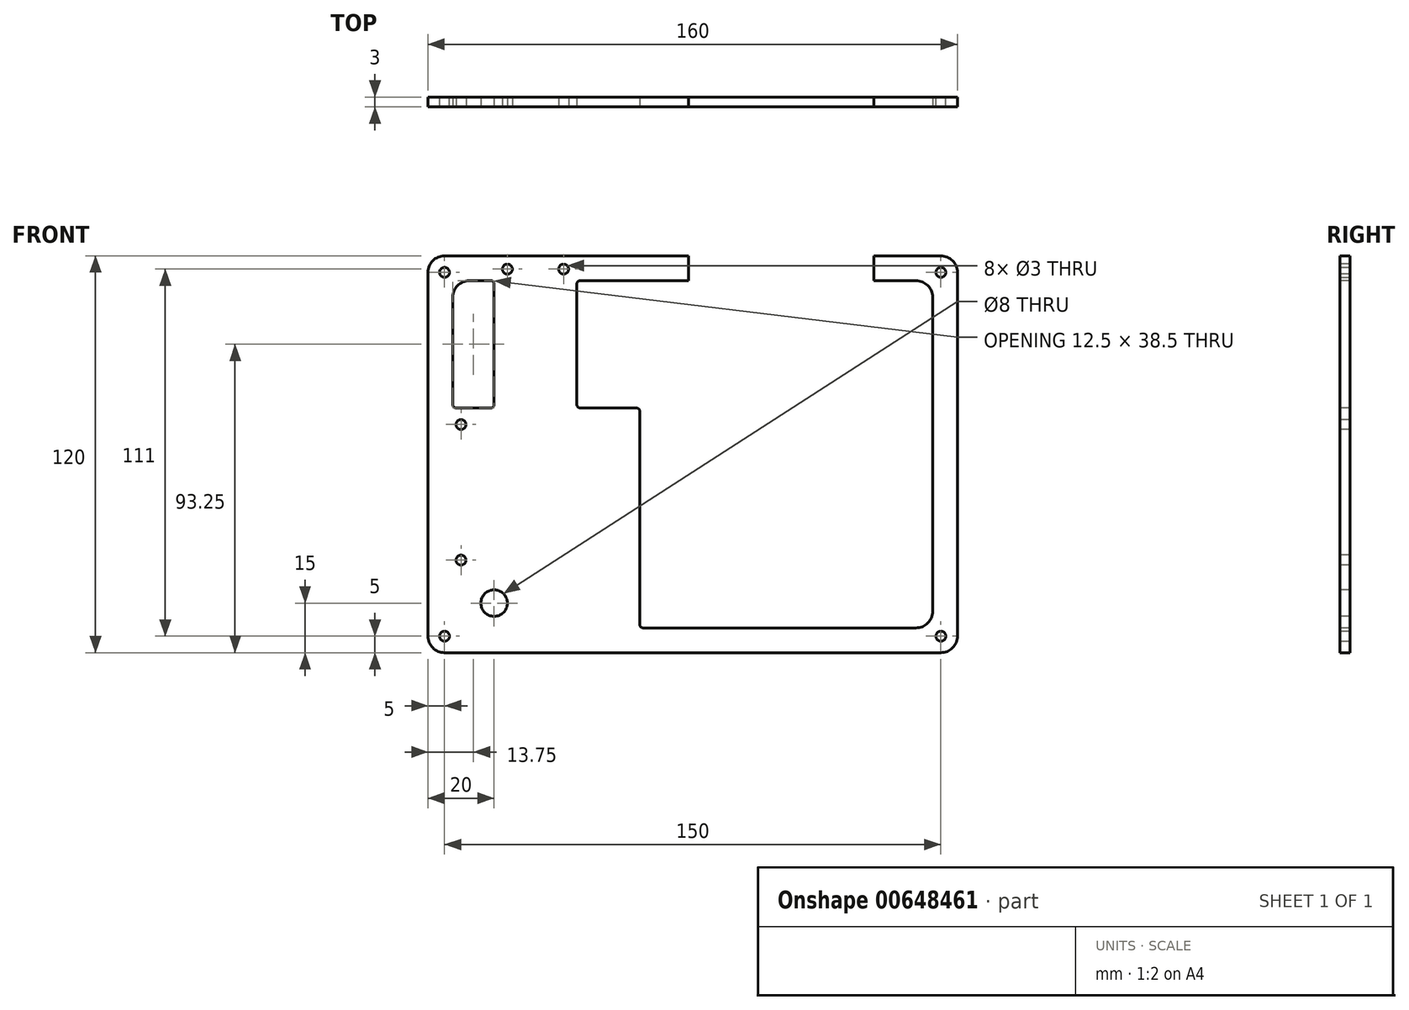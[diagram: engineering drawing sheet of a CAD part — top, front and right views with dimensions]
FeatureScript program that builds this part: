
annotation { "Feature Type Name" : "Feature", "Feature Type Description" : "" }
export const myFeature = defineFeature(function(context is Context, id is Id, definition is map)
    precondition{}
    {
        {
            var Q0;
            Q0=qCreatedBy(makeId("Front.planeOp"),FACE);
            var sketch = newSketch(context, id + "F0", { "sketchPlane" : qUnion([Q0])});
            skLineSegment(sketch, "E0.bottom", {"start": v(75, -60) * mm, "end": v(-75, -60) * mm});
            skLineSegment(sketch, "E0.top", {"start": v(75, 60) * mm, "end": v(-75, 60) * mm});
            skLineSegment(sketch, "E0.left", {"start": v(80, -55) * mm, "end": v(80, 55) * mm});
            skLineSegment(sketch, "E0.right", {"start": v(-80, -55) * mm, "end": v(-80, 55) * mm});
            skPoint(sketch, "E0.middle", {"position": v(0, 0) * mm});
            skPoint(sketch, "E1.visualSharp", {"position": v(-80, 60) * mm});
            skArc(sketch, "E1.filletArc", {"start": v(-75, 60) * mm, "mid": v(-78.54, 58.54) * mm, "end": v(-80, 55) * mm});
            skPoint(sketch, "E2.visualSharp", {"position": v(80, 60) * mm});
            skArc(sketch, "E2.filletArc", {"start": v(80, 55) * mm, "mid": v(78.54, 58.54) * mm, "end": v(75, 60) * mm});
            skPoint(sketch, "E3.visualSharp", {"position": v(80, -60) * mm});
            skArc(sketch, "E3.filletArc", {"start": v(75, -60) * mm, "mid": v(78.54, -58.54) * mm, "end": v(80, -55) * mm});
            skPoint(sketch, "E4.visualSharp", {"position": v(-80, -60) * mm});
            skArc(sketch, "E4.filletArc", {"start": v(-80, -55) * mm, "mid": v(-78.54, -58.54) * mm, "end": v(-75, -60) * mm});
            skSolve(sketch);
        }
        {
            var Q0;
            Q0=makeQuery(id+"F0.imprint","IMPRINT",FACE,{"disambiguationData":[TD([[makeQuery(id+"F0.imprint","IMPRINT",EDGE,{"derivedFrom":sQuery(id+"F0.wireOp",EDGE,"E0.bottom")}),-1.0]])]});
            extrude(context, id + "F1", {"entities" : qUnion([Q0]), "depth" : 3 * mm, "offsetDistance" : 25 * mm});
        }
        {
            var Q0;
            Q0=qCreatedBy(makeId("Front.planeOp"),FACE);
            var sketch = newSketch(context, id + "F2", { "sketchPlane" : qUnion([Q0])});
            skCircle(sketch, "E5", {"center": v(-75, 55) * mm, "radius": 1.5 * mm});
            skCircle(sketch, "E6", {"center": v(75, 55) * mm, "radius": 1.5 * mm});
            skCircle(sketch, "E7", {"center": v(75, -55) * mm, "radius": 1.5 * mm});
            skCircle(sketch, "E8", {"center": v(-75, -55) * mm, "radius": 1.5 * mm});
            skSolve(sketch);
        }
        {
            var Q0;
            Q0=qSketchRegion(id+"F2",true);
            extrude(context, id + "F3", {"entities" : qUnion([Q0]), "operationType" : NewBodyOperationType.REMOVE, "depth" : 25 * mm, "offsetDistance" : 25 * mm});
        }
        {
            var Q0;
            Q0=makeQuery(id+"F1.opExtrude","CAP_FACE",FACE,{"disambiguationData":[OSD([sQuery(id+"F0.wireOp",EDGE,"E0.bottom"),sQuery(id+"F0.wireOp",EDGE,"E0.top"),sQuery(id+"F0.wireOp",EDGE,"E0.left"),sQuery(id+"F0.wireOp",EDGE,"E0.right"),sQuery(id+"F0.wireOp",EDGE,"E1.filletArc"),sQuery(id+"F0.wireOp",EDGE,"E2.filletArc"),sQuery(id+"F0.wireOp",EDGE,"E3.filletArc"),sQuery(id+"F0.wireOp",EDGE,"E4.filletArc")])],"isStart":false});
            var sketch = newSketch(context, id + "F4", { "sketchPlane" : qUnion([Q0])});
            skLineSegment(sketch, "E9.bottom", {"start": v(67.5, 52.5) * mm, "end": v(54.75, 52.5) * mm});
            skLineSegment(sketch, "E9.top", {"start": v(67.5, -52.5) * mm, "end": v(-15, -52.5) * mm});
            skLineSegment(sketch, "E9.left", {"start": v(72.5, 47.5) * mm, "end": v(72.5, -47.5) * mm});
            skLineSegment(sketch, "E9.right", {"start": v(-72.5, 47.5) * mm, "end": v(-72.5, 15) * mm});
            skPoint(sketch, "E9.middle", {"position": v(0, 0) * mm});
            skPoint(sketch, "E10.visualSharp", {"position": v(-72.5, 52.5) * mm});
            skArc(sketch, "E10.filletArc", {"start": v(-67.5, 52.5) * mm, "mid": v(-71.04, 51.04) * mm, "end": v(-72.5, 47.5) * mm});
            skPoint(sketch, "E11.visualSharp", {"position": v(72.5, 52.5) * mm});
            skArc(sketch, "E11.filletArc", {"start": v(72.5, 47.5) * mm, "mid": v(71.04, 51.04) * mm, "end": v(67.5, 52.5) * mm});
            skPoint(sketch, "E12.visualSharp", {"position": v(72.5, -52.5) * mm});
            skArc(sketch, "E12.filletArc", {"start": v(67.5, -52.5) * mm, "mid": v(71.04, -51.04) * mm, "end": v(72.5, -47.5) * mm});
            skLineSegment(sketch, "E13", {"start": v(-71.5, 14) * mm, "end": v(-61, 14) * mm});
            skLineSegment(sketch, "E14", {"start": v(-16, 13) * mm, "end": v(-16, -51.5) * mm});
            skPoint(sketch, "E15.visualSharp", {"position": v(-16, 14) * mm});
            skArc(sketch, "E15.filletArc", {"start": v(-16, 13) * mm, "mid": v(-16.3, 13.7) * mm, "end": v(-17, 14) * mm});
            skPoint(sketch, "E16.visualSharp", {"position": v(-72.5, 14) * mm});
            skArc(sketch, "E16.filletArc", {"start": v(-72.5, 15) * mm, "mid": v(-72.2, 14.3) * mm, "end": v(-71.5, 14) * mm});
            skPoint(sketch, "E17.visualSharp", {"position": v(-16, -52.5) * mm});
            skArc(sketch, "E17.filletArc", {"start": v(-16, -51.5) * mm, "mid": v(-15.7, -52.2) * mm, "end": v(-15, -52.5) * mm});
            skLineSegment(sketch, "E18", {"start": v(-60, 51.5) * mm, "end": v(-60, 15) * mm});
            skLineSegment(sketch, "E19", {"start": v(-35, 51.5) * mm, "end": v(-35, 15) * mm});
            skLineSegment(sketch, "E20.trimOffspring", {"start": v(-61, 52.5) * mm, "end": v(-67.5, 52.5) * mm});
            skPoint(sketch, "E21.visualSharp", {"position": v(-35, 52.5) * mm});
            skArc(sketch, "E21.filletArc", {"start": v(-34, 52.5) * mm, "mid": v(-34.7, 52.2) * mm, "end": v(-35, 51.5) * mm});
            skPoint(sketch, "E22.visualSharp", {"position": v(-60, 52.5) * mm});
            skArc(sketch, "E22.filletArc", {"start": v(-60, 51.5) * mm, "mid": v(-60.3, 52.2) * mm, "end": v(-61, 52.5) * mm});
            skLineSegment(sketch, "E23.trimOffspring", {"start": v(-34, 14) * mm, "end": v(-17, 14) * mm});
            skPoint(sketch, "E24.visualSharp", {"position": v(-60, 14) * mm});
            skArc(sketch, "E24.filletArc", {"start": v(-61, 14) * mm, "mid": v(-60.3, 14.3) * mm, "end": v(-60, 15) * mm});
            skPoint(sketch, "E25.visualSharp", {"position": v(-35, 14) * mm});
            skArc(sketch, "E25.filletArc", {"start": v(-35, 15) * mm, "mid": v(-34.7, 14.3) * mm, "end": v(-34, 14) * mm});
            skLineSegment(sketch, "E26", {"start": v(-1.25, 60) * mm, "end": v(-1.25, 52.5) * mm});
            skLineSegment(sketch, "E27", {"start": v(54.75, 60) * mm, "end": v(54.75, 52.5) * mm});
            skLineSegment(sketch, "E28.0.0", {"start": v(54.75, 60) * mm, "end": v(-1.25, 60) * mm});
            skLineSegment(sketch, "E28.0.2", {"start": v(-1.25, 60) * mm, "end": v(54.75, 60) * mm});
            skPoint(sketch, "E29.orphan", {"position": v(-75, 60) * mm});
            skPoint(sketch, "E30.orphan", {"position": v(75, 60) * mm});
            skLineSegment(sketch, "E31.trimOffspring", {"start": v(-1.25, 52.5) * mm, "end": v(-34, 52.5) * mm});
            skSolve(sketch);
        }
        {
            var Q0;
            Q0=makeQuery(id+"F4.imprint","IMPRINT",FACE,{"disambiguationData":[TD([[makeQuery(id+"F4.imprint","IMPRINT",EDGE,{"derivedFrom":sQuery(id+"F4.wireOp",EDGE,"E9.bottom")}),1.0]])]});
            extrude(context, id + "F5", {"entities" : qUnion([Q0]), "operationType" : NewBodyOperationType.REMOVE, "oppositeDirection" : true, "depth" : 3 * mm, "offsetDistance" : 25 * mm});
        }
        {
            var Q0;
            Q0=makeQuery(id+"F1.opExtrude","CAP_FACE",FACE,{"disambiguationData":[OSD([sQuery(id+"F0.wireOp",EDGE,"E0.bottom"),sQuery(id+"F0.wireOp",EDGE,"E0.top"),sQuery(id+"F0.wireOp",EDGE,"E0.left"),sQuery(id+"F0.wireOp",EDGE,"E0.right"),sQuery(id+"F0.wireOp",EDGE,"E1.filletArc"),sQuery(id+"F0.wireOp",EDGE,"E2.filletArc"),sQuery(id+"F0.wireOp",EDGE,"E3.filletArc"),sQuery(id+"F0.wireOp",EDGE,"E4.filletArc")])],"isStart":false});
            var sketch = newSketch(context, id + "F6", { "sketchPlane" : qUnion([Q0])});
            skCircle(sketch, "E32", {"center": v(-56, 56) * mm, "radius": 1.5 * mm});
            skCircle(sketch, "E33", {"center": v(-39, 56) * mm, "radius": 1.5 * mm});
            skSolve(sketch);
        }
        {
            var Q0;
            Q0=sQuery(id+"F6.wireOp",VERTEX,"E32.center");
            var Q1;
            Q1=sQuery(id+"F6.wireOp",VERTEX,"E33.center");
            var Q2;
            Q2=makeQuery(id+"F1.opExtrude","SWEPT_BODY",BODY,{"disambiguationData":[OSD([sQuery(id+"F0.wireOp",EDGE,"E0.bottom"),sQuery(id+"F0.wireOp",EDGE,"E0.top"),sQuery(id+"F0.wireOp",EDGE,"E0.left"),sQuery(id+"F0.wireOp",EDGE,"E0.right"),sQuery(id+"F0.wireOp",EDGE,"E1.filletArc"),sQuery(id+"F0.wireOp",EDGE,"E2.filletArc"),sQuery(id+"F0.wireOp",EDGE,"E3.filletArc"),sQuery(id+"F0.wireOp",EDGE,"E4.filletArc")])]});
            hole(context, id + "F7", {"style" : HoleStyle.SIMPLE, "endStyle" : HoleEndStyle.BLIND, "holeDiameter" : 3 * mm, "majorDiameter" : 5 * mm, "holeDepth" : 3 * mm, "isTappedThrough" : true, "tappedDepth" : 12 * mm, "tapClearance" : 3, "startFromSketch" : true, "locations" : qUnion([Q0, Q1]), "scope" : qUnion([Q2])});
        }
        {
            var Q0;
            Q0 = qSketchRegion(id + "F4", true);
            extrude(context, id + "F8", {"entities" : qUnion([Q0]), "operationType" : NewBodyOperationType.REMOVE, "oppositeDirection" : true, "depth" : 3 * mm, "offsetDistance" : 25 * mm});
        }
        {
            var Q0;
            Q0=makeQuery(id+"F1.opExtrude","CAP_FACE",FACE,{"disambiguationData":[OSD([sQuery(id+"F0.wireOp",EDGE,"E0.bottom"),sQuery(id+"F0.wireOp",EDGE,"E0.top"),sQuery(id+"F0.wireOp",EDGE,"E0.left"),sQuery(id+"F0.wireOp",EDGE,"E0.right"),sQuery(id+"F0.wireOp",EDGE,"E1.filletArc"),sQuery(id+"F0.wireOp",EDGE,"E2.filletArc"),sQuery(id+"F0.wireOp",EDGE,"E3.filletArc"),sQuery(id+"F0.wireOp",EDGE,"E4.filletArc")])],"isStart":false});
            var sketch = newSketch(context, id + "F9", { "sketchPlane" : qUnion([Q0])});
            skCircle(sketch, "E34", {"center": v(-70, 9) * mm, "radius": 1.5 * mm});
            skCircle(sketch, "E35", {"center": v(-70, -32) * mm, "radius": 1.5 * mm});
            skCircle(sketch, "E36", {"center": v(-60, -45) * mm, "radius": 4 * mm});
            skSolve(sketch);
        }
        {
            var Q0;
            Q0=makeQuery(id+"F9.imprint","IMPRINT",FACE,{"disambiguationData":[TD([[makeQuery(id+"F9.imprint","IMPRINT",EDGE,{"derivedFrom":sQuery(id+"F9.wireOp",EDGE,"E34")}),1.0]])]});
            var Q1;
            Q1=makeQuery(id+"F9.imprint","IMPRINT",FACE,{"disambiguationData":[TD([[makeQuery(id+"F9.imprint","IMPRINT",EDGE,{"derivedFrom":sQuery(id+"F9.wireOp",EDGE,"WX1qEks4-UDcN-zf3z-NcHy-JZ1I9pBFhsB6")}),1.0]])]});
            var Q2;
            Q2=makeQuery(id+"F9.imprint","IMPRINT",FACE,{"disambiguationData":[TD([[makeQuery(id+"F9.imprint","IMPRINT",EDGE,{"derivedFrom":sQuery(id+"F9.wireOp",EDGE,"E36")}),1.0]])]});
            var Q3;
            Q3=makeQuery(id+"F9.imprint","IMPRINT",FACE,{"disambiguationData":[TD([[makeQuery(id+"F9.imprint","IMPRINT",EDGE,{"derivedFrom":sQuery(id+"F9.wireOp",EDGE,"E35")}),1.0]])]});
            extrude(context, id + "F10", {"entities" : qUnion([Q0, Q1, Q2, Q3]), "operationType" : NewBodyOperationType.REMOVE, "oppositeDirection" : true, "depth" : 25 * mm, "offsetDistance" : 25 * mm});
        }
    });
